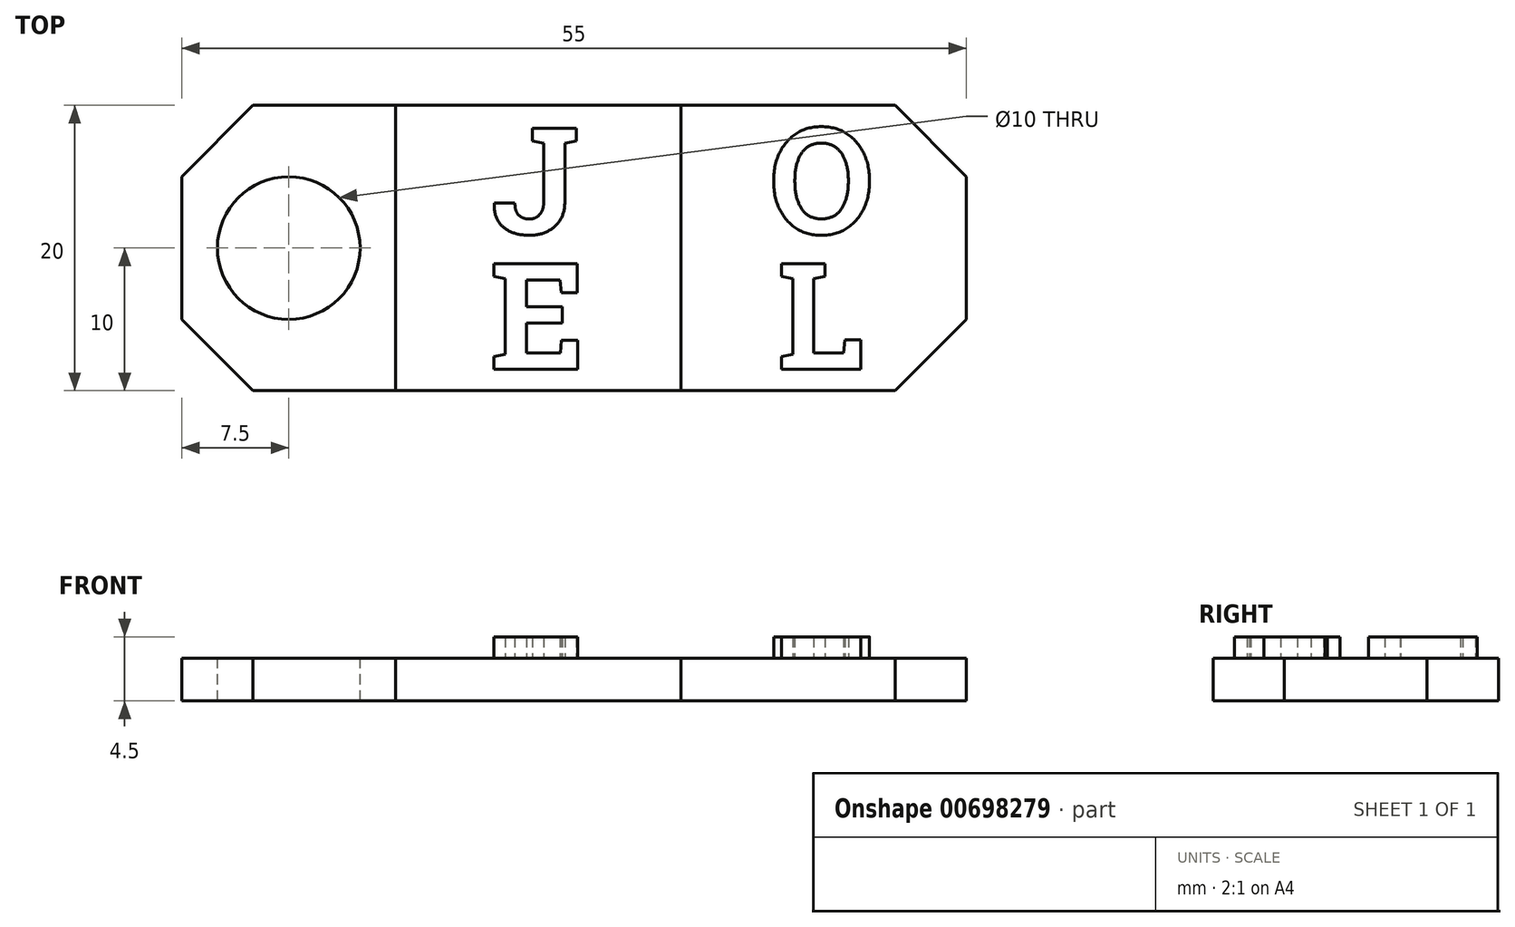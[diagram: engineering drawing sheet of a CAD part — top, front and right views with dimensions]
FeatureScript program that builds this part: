
annotation { "Feature Type Name" : "Feature", "Feature Type Description" : "" }
export const myFeature = defineFeature(function(context is Context, id is Id, definition is map)
    precondition{}
    {
        {
            var Q0;
            Q0=qCreatedBy(makeId("Top.planeOp"),FACE);
            var sketch = newSketch(context, id + "F0", { "sketchPlane" : qUnion([Q0])});
            skLineSegment(sketch, "E0.bottom", {"start": v(-10, 10) * mm, "end": v(10, 10) * mm});
            skLineSegment(sketch, "E0.top", {"start": v(-10, -10) * mm, "end": v(10, -10) * mm});
            skLineSegment(sketch, "E0.left", {"start": v(-10, 10) * mm, "end": v(-10, -10) * mm});
            skLineSegment(sketch, "E0.right", {"start": v(10, 10) * mm, "end": v(10, -10) * mm});
            skSolve(sketch);
        }
        {
            var Q0;
            Q0 = qSketchRegion(id + "F0", true);
            extrude(context, id + "F1", {"entities" : qUnion([Q0]), "depth" : 3 * mm, "offsetDistance" : 25 * mm});
        }
        {
            var Q0;
            Q0=makeQuery(id+"F1.opExtrude","CAP_FACE",FACE,{"disambiguationData":[OSD([sQuery(id+"F0.wireOp",EDGE,"E0.bottom"),sQuery(id+"F0.wireOp",EDGE,"E0.top"),sQuery(id+"F0.wireOp",EDGE,"E0.left"),sQuery(id+"F0.wireOp",EDGE,"E0.right")])],"isStart":false});
            var sketch = newSketch(context, id + "F2", { "sketchPlane" : qUnion([Q0])});
            skLineSegment(sketch, "E1", {"start": v(-10, 10) * mm, "end": v(-30, 10) * mm});
            skLineSegment(sketch, "E2", {"start": v(-30, 10) * mm, "end": v(-30, -10) * mm});
            skLineSegment(sketch, "E3", {"start": v(-10, -10) * mm, "end": v(-30, -10) * mm});
            skLineSegment(sketch, "E4", {"start": v(-10, 10) * mm, "end": v(-10, -10) * mm});
            skSolve(sketch);
        }
        {
            var Q0;
            Q0 = qSketchRegion(id + "F2", true);
            extrude(context, id + "F3", {"entities" : qUnion([Q0]), "oppositeDirection" : true, "depth" : 3 * mm, "offsetDistance" : 25 * mm});
        }
        {
            var Q0;
            Q0=makeQuery(id+"F3.opExtrude","CAP_FACE",FACE,{"disambiguationData":[OSD([sQuery(id+"F2.wireOp",EDGE,"E1"),sQuery(id+"F2.wireOp",EDGE,"E2"),sQuery(id+"F2.wireOp",EDGE,"E3"),sQuery(id+"F2.wireOp",EDGE,"E4")])],"isStart":true});
            var sketch = newSketch(context, id + "F4", { "sketchPlane" : qUnion([Q0])});
            skLineSegment(sketch, "E5", {"start": v(-30, 10) * mm, "end": v(-30, -10) * mm});
            skLineSegment(sketch, "E6", {"start": v(-30, -10) * mm, "end": v(-45, -10) * mm});
            skLineSegment(sketch, "E7", {"start": v(-30, 10) * mm, "end": v(-45, 10) * mm});
            skLineSegment(sketch, "E8", {"start": v(-45, -10) * mm, "end": v(-45, 10) * mm});
            skSolve(sketch);
        }
        {
            var Q0;
            Q0 = qSketchRegion(id + "F4", true);
            extrude(context, id + "F5", {"entities" : qUnion([Q0]), "oppositeDirection" : true, "depth" : 3 * mm, "offsetDistance" : 25 * mm});
        }
        {
            var Q0;
            Q0=makeQuery(id+"F5.opExtrude","CAP_FACE",FACE,{"disambiguationData":[OSD([sQuery(id+"F4.wireOp",EDGE,"E5"),sQuery(id+"F4.wireOp",EDGE,"E6"),sQuery(id+"F4.wireOp",EDGE,"E7"),sQuery(id+"F4.wireOp",EDGE,"E8")])],"isStart":true});
            var sketch = newSketch(context, id + "F6", { "sketchPlane" : qUnion([Q0])});
            skLineSegment(sketch, "E9", {"start": v(-37.5, 10) * mm, "end": v(-37.5, -10) * mm, "construction": true});
            skCircle(sketch, "E10", {"center": v(-37.5, 0) * mm, "radius": 5 * mm});
            skSolve(sketch);
        }
        {
            var Q0;
            Q0 = qSketchRegion(id + "F6", true);
            extrude(context, id + "F7", {"entities" : qUnion([Q0]), "operationType" : NewBodyOperationType.REMOVE, "endBound" : BoundingType.THROUGH_ALL, "oppositeDirection" : true, "depth" : 25 * mm, "offsetDistance" : 25 * mm});
        }
        {
            var Q0;
            Q0=makeQuery(id+"F3.opExtrude","CAP_FACE",FACE,{"disambiguationData":[OSD([sQuery(id+"F2.wireOp",EDGE,"E1"),sQuery(id+"F2.wireOp",EDGE,"E2"),sQuery(id+"F2.wireOp",EDGE,"E3"),sQuery(id+"F2.wireOp",EDGE,"E4")])],"isStart":true});
            var sketch = newSketch(context, id + "F8", { "sketchPlane" : qUnion([Q0])});
            skLineSegment(sketch, "E11", {"start": v(-10, 8.5) * mm, "end": v(-30, 8.5) * mm, "construction": true});
            skLineSegment(sketch, "E12", {"start": v(-10, 1) * mm, "end": v(-30, 1) * mm, "construction": true});
            skLineSegment(sketch, "E13", {"start": v(-10, -1) * mm, "end": v(-30, -1) * mm, "construction": true});
            skLineSegment(sketch, "E14", {"start": v(-10, -8.5) * mm, "end": v(-30, -8.5) * mm, "construction": true});
            skText(sketch, "E15", { "text": "J", "fontName": "RobotoSlab-Bold.ttf"});
            skText(sketch, "E16", { "text": "E", "fontName": "RobotoSlab-Bold.ttf"});
            const initialGuessF8  = {"E15": [-0.02328, 0.001, 1, 0, 0.0075], "E16": [-0.0234, -0.0085, 1, 0, 0.0075]};
            skSetInitialGuess(sketch, initialGuessF8);
            skSolve(sketch);
        }
        {
            var Q0;
            Q0 = qSketchRegion(id + "F8", true);
            extrude(context, id + "F9", {"entities" : qUnion([Q0]), "operationType" : NewBodyOperationType.ADD, "depth" : 1.5 * mm, "offsetDistance" : 25 * mm});
        }
        {
            var Q0;
            Q0=makeQuery(id+"F1.opExtrude","CAP_FACE",FACE,{"disambiguationData":[OSD([sQuery(id+"F0.wireOp",EDGE,"E0.bottom"),sQuery(id+"F0.wireOp",EDGE,"E0.top"),sQuery(id+"F0.wireOp",EDGE,"E0.left"),sQuery(id+"F0.wireOp",EDGE,"E0.right")])],"isStart":false});
            var sketch = newSketch(context, id + "F10", { "sketchPlane" : qUnion([Q0])});
            skLineSegment(sketch, "E17", {"start": v(10, 8.5) * mm, "end": v(-10, 8.5) * mm, "construction": true});
            skLineSegment(sketch, "E18", {"start": v(10, 1) * mm, "end": v(-10, 1) * mm, "construction": true});
            skLineSegment(sketch, "E19", {"start": v(10, -1) * mm, "end": v(-10, -1) * mm, "construction": true});
            skLineSegment(sketch, "E20", {"start": v(10, -8.5) * mm, "end": v(-10, -8.5) * mm, "construction": true});
            skText(sketch, "E21", { "text": "O", "fontName": "RobotoSlab-Bold.ttf"});
            skText(sketch, "E22", { "text": "L", "fontName": "RobotoSlab-Bold.ttf"});
            const initialGuessF10  = {"E21": [-0.00385, 0.001, 1, 0, 0.0075], "E22": [-0.00325, -0.0085, 1, 0, 0.0075]};
            skSetInitialGuess(sketch, initialGuessF10);
            skSolve(sketch);
        }
        {
            var Q0;
            Q0 = qSketchRegion(id + "F10", true);
            extrude(context, id + "F11", {"entities" : qUnion([Q0]), "operationType" : NewBodyOperationType.ADD, "depth" : 1.5 * mm, "offsetDistance" : 25 * mm});
        }
        {
            var Q0;
            Q0=makeQuery(id+"F1.opExtrude","SWEPT_EDGE",EDGE,{"disambiguationData":[OSD([sQuery(id+"F0.wireOp",EDGE,"E0.top"),sQuery(id+"F0.wireOp",EDGE,"E0.right")])]});
            var Q1;
            Q1=makeQuery(id+"F1.opExtrude","SWEPT_EDGE",EDGE,{"disambiguationData":[OSD([sQuery(id+"F0.wireOp",EDGE,"E0.bottom"),sQuery(id+"F0.wireOp",EDGE,"E0.right")])]});
            var Q2;
            Q2=makeQuery(id+"F5.opExtrude","SWEPT_EDGE",EDGE,{"disambiguationData":[OSD([sQuery(id+"F4.wireOp",EDGE,"E7"),sQuery(id+"F4.wireOp",EDGE,"E8")])]});
            var Q3;
            Q3=makeQuery(id+"F5.opExtrude","SWEPT_EDGE",EDGE,{"disambiguationData":[OSD([sQuery(id+"F4.wireOp",EDGE,"E6"),sQuery(id+"F4.wireOp",EDGE,"E8")])]});
            chamfer(context, id + "F12", {"entities" : qUnion([Q0, Q1, Q2, Q3]), "width" : 5 * mm, "tangentPropagation" : true});
        }
    });
